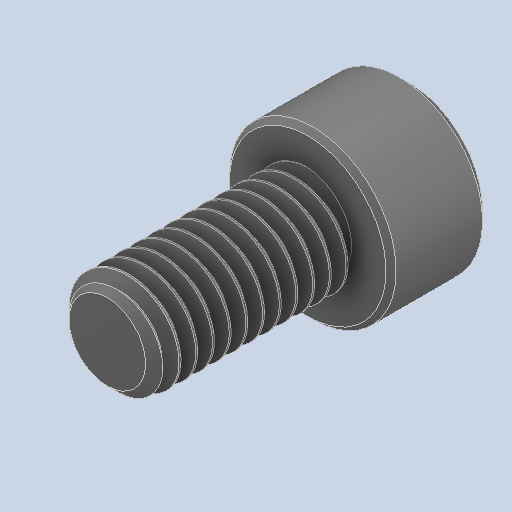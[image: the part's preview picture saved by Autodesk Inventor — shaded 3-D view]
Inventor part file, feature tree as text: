
AUTODESK INVENTOR PART (.ipt)
format: ipt  version: 2023.2 (Build 272271000, 271)  size: 523,264 bytes
history: native  units: in
note: dims shown in document units (in); Inventor stores cm internally (conversion verified against a paired STEP export)
features: chamfer x1
ambient origin geometry x8: Origin, YZ Plane, XZ Plane, XY Plane, X Axis, Y Axis, Z Axis, Center Point
bodies: Solid1 (feature_tree)
feature tree (1):
  chamfer  "Chamfer2"  [1 undecoded]
note: 1 required parameter value undecoded (feature->parameter linkage not recoverable at this tier; creation-order binding heuristic only, values carry confidence <= 0.55)
